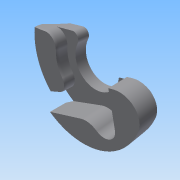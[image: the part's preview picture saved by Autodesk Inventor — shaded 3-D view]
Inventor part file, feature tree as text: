
AUTODESK INVENTOR PART (.ipt)
format: ipt  version: 2015 (Build 190159000, 159)  size: 212,992 bytes
history: native  units: in
note: dims shown in document units (in); Inventor stores cm internally (conversion verified against a paired STEP export)
features: extrude x4, fillet x4, sketch x3, other x2, chamfer x2, mirror x1
ambient origin geometry x8: Origin, YZ Plane, XZ Plane, XY Plane, X Axis, Y Axis, Z Axis, Center Point
bodies: Solid1 (feature_tree)
feature tree (16):
  other  "mount_alt.ipt"
  other  "mount_sketch_alt.ipt"
  sketch  "Sketch2"  dims[d0=0.3937in d1=0.3937in]
  extrude  "Extrusion1"  Depth=0.3937in
  extrude  "Extrusion2"  Depth=0.9843in
  extrude  "Extrusion3"  Depth=0.3875in TaperAngle=0.0deg
  fillet  "Fillet1"  Radius=0.5in
  chamfer  "Chamfer1"  Distance=0.125in
  fillet  "Fillet2"  Radius=0.01in
  fillet  "Fillet3"  Radius=0.2in
  chamfer  "Chamfer2"  Distance=0.3875in
  extrude  "Extrusion4"  Depth=0.3875in TaperAngle=45.0deg
  fillet  "Fillet4"  Radius=0.5in
  mirror  "Mirror1"
  sketch  "Sketch15"  dims[d4=0.25in d5=0.0in d6=0.25in d7=0.0in d8=0.5in d9=0.0in d10=0.125in d11=0.01in d12=0.125in d13=45.0deg d14=0.2in d15=0.3875in d16=0.35in d17=0.125in d18=45.0deg d19=0.5in d20=0.0in d21=0.3875in]
  sketch  "Sketch3"  dims[d2=2.6251in d3=0.9843in]
